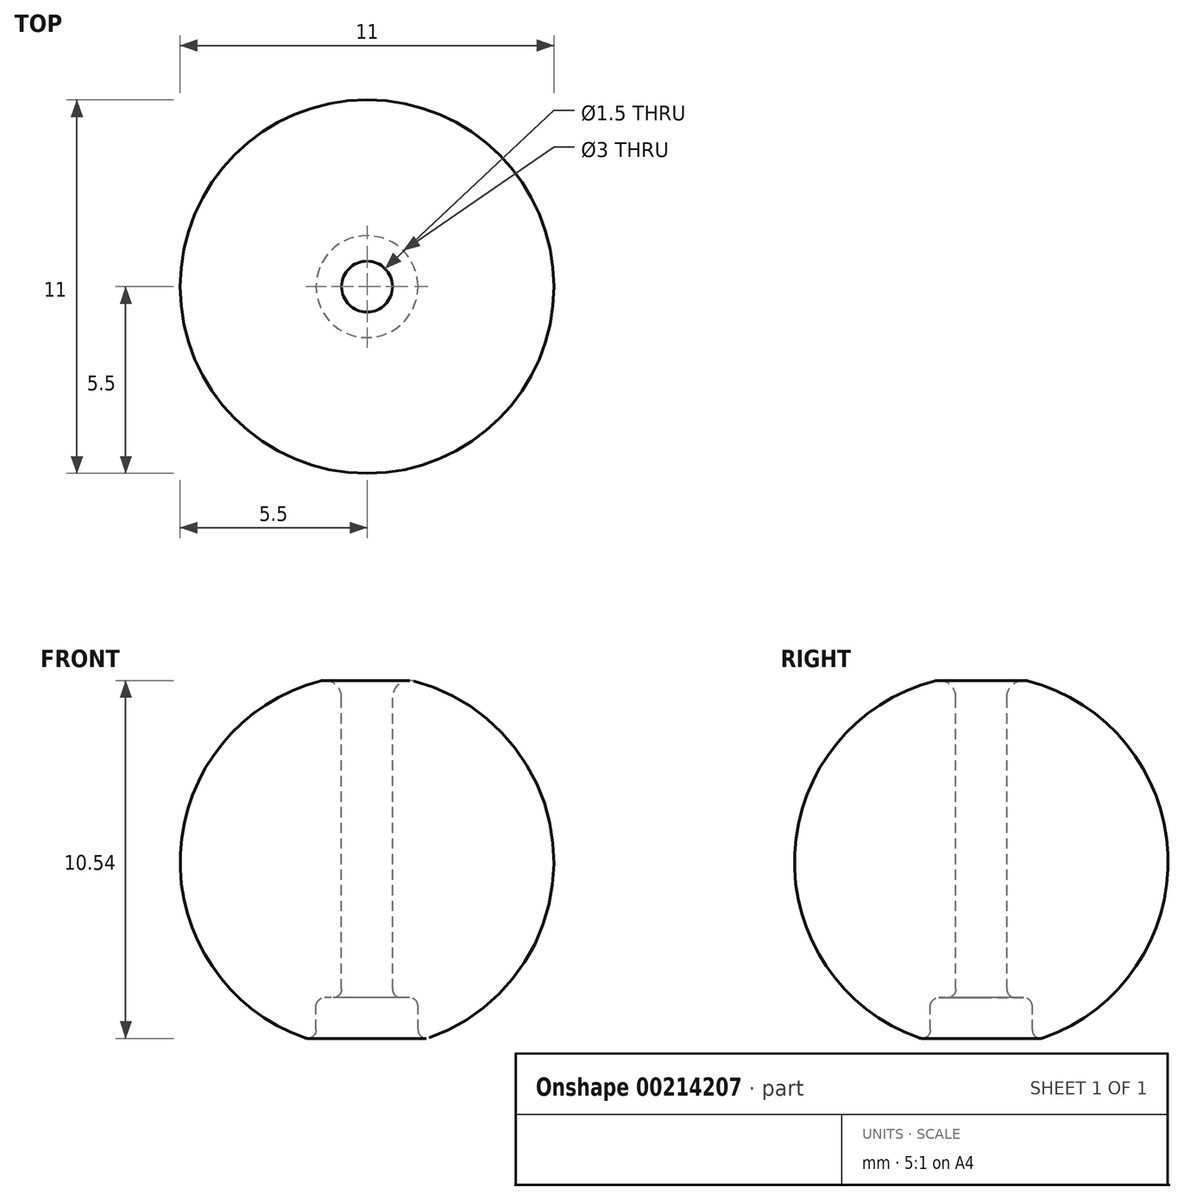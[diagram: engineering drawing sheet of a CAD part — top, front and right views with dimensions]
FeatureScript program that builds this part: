
annotation { "Feature Type Name" : "Feature", "Feature Type Description" : "" }
export const myFeature = defineFeature(function(context is Context, id is Id, definition is map)
    precondition{}
    {
        {
            var Q0;
            Q0=qCreatedBy(makeId("Front.planeOp"),FACE);
            var sketch = newSketch(context, id + "F0", { "sketchPlane" : qUnion([Q0])});
            skLineSegment(sketch, "E0", {"start": v(0, 12.7) * mm, "end": v(0, -11.2) * mm, "construction": true});
            skArc(sketch, "E1", {"start": v(-1.38, 5.33) * mm, "mid": v(-5.5, 0.24) * mm, "end": v(-1.83, -5.19) * mm});
            skLineSegment(sketch, "E2", {"start": v(-0.75, 4.84) * mm, "end": v(-0.75, -3.75) * mm});
            skLineSegment(sketch, "E3", {"start": v(-1, -4) * mm, "end": v(-1.25, -4) * mm});
            skLineSegment(sketch, "E4", {"start": v(-1.5, -4.25) * mm, "end": v(-1.5, -4.95) * mm});
            skArc(sketch, "E5.filletArc", {"start": v(-0.75, 4.84) * mm, "mid": v(-0.94, 5.24) * mm, "end": v(-1.37, 5.33) * mm});
            skPoint(sketch, "E6.orphan", {"position": v(0, -5.5) * mm});
            skPoint(sketch, "E7.visualSharp", {"position": v(-1.5, -5.3) * mm});
            skArc(sketch, "E7.filletArc", {"start": v(-1.83, -5.19) * mm, "mid": v(-1.6, -5.15) * mm, "end": v(-1.5, -4.95) * mm});
            skPoint(sketch, "E8.visualSharp", {"position": v(-0.75, -4) * mm});
            skArc(sketch, "E8.filletArc", {"start": v(-1, -4) * mm, "mid": v(-0.82, -3.93) * mm, "end": v(-0.75, -3.75) * mm});
            skPoint(sketch, "E9.visualSharp", {"position": v(-1.5, -4) * mm});
            skArc(sketch, "E9.filletArc", {"start": v(-1.25, -4) * mm, "mid": v(-1.43, -4.07) * mm, "end": v(-1.5, -4.25) * mm});
            skSolve(sketch);
        }
        {
            var Q0;
            Q0=makeQuery(id+"F0.imprint","IMPRINT",FACE,{"disambiguationData":[TD([[makeQuery(id+"F0.imprint","IMPRINT",EDGE,{"derivedFrom":sQuery(id+"F0.wireOp",EDGE,"E1")}),1.0]])]});
            var Q1;
            Q1=sQuery(id+"F0.wireOp",EDGE,"E0");
            revolve(context, id + "F1", {"entities" : qUnion([Q0]), "axis" : qUnion([Q1]), "revolveType" : RevolveType.FULL});
        }
    });
